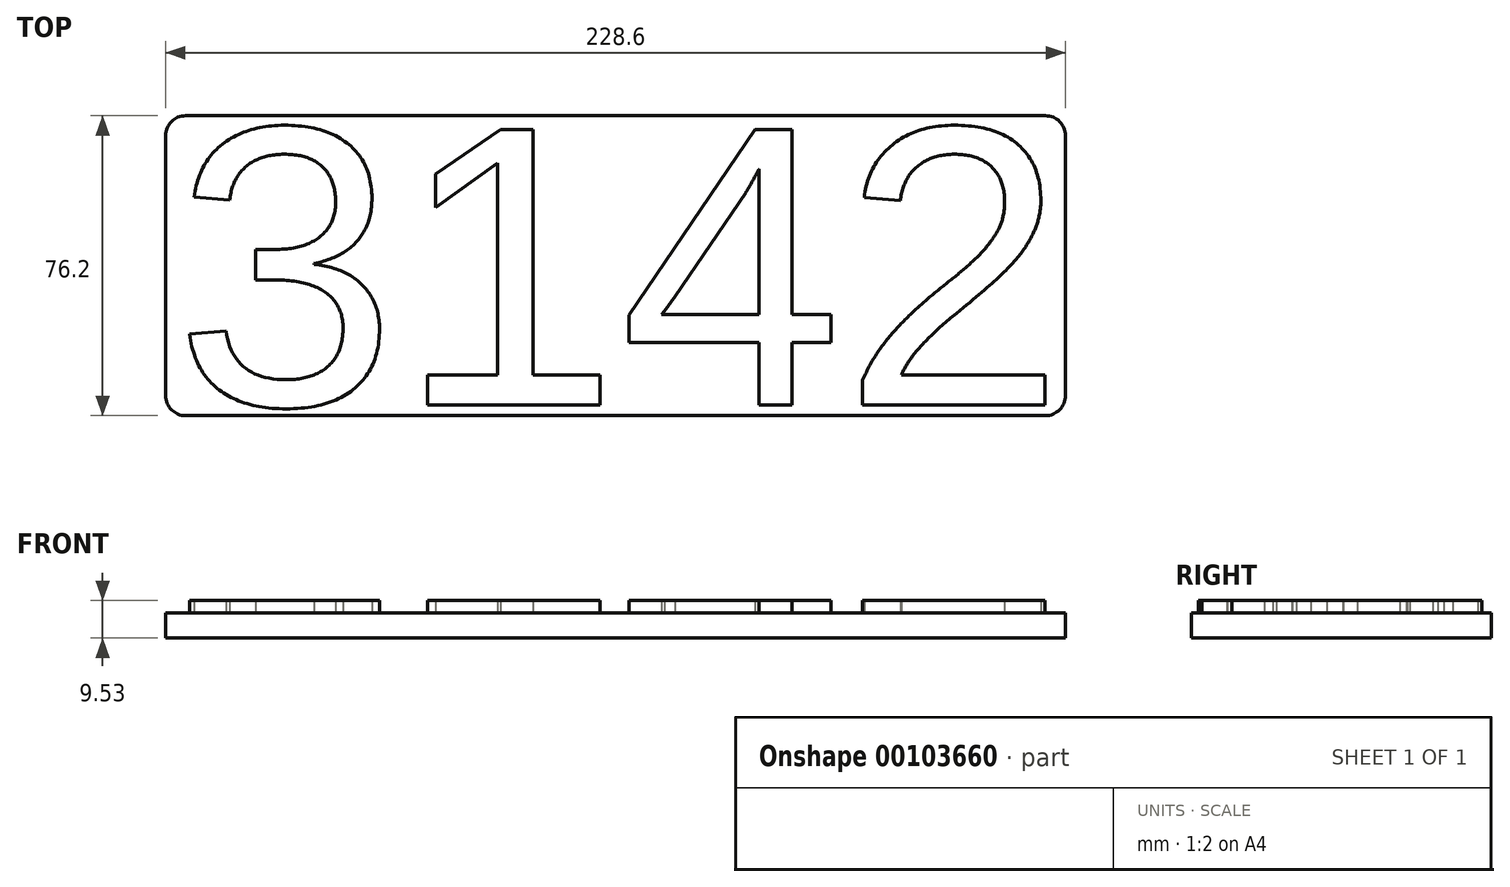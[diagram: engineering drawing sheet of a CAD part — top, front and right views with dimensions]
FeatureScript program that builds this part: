
annotation { "Feature Type Name" : "Feature", "Feature Type Description" : "" }
export const myFeature = defineFeature(function(context is Context, id is Id, definition is map)
    precondition{}
    {
        {
            var Q0;
            Q0=qCreatedBy(makeId("Top.planeOp"),FACE);
            var sketch = newSketch(context, id + "F0", { "sketchPlane" : qUnion([Q0])});
            skLineSegment(sketch, "E0.bottom", {"start": v(-101.24, 50.27) * mm, "end": v(127.36, 50.27) * mm});
            skLineSegment(sketch, "E0.top", {"start": v(-101.24, -25.93) * mm, "end": v(127.36, -25.93) * mm});
            skLineSegment(sketch, "E0.left", {"start": v(-101.24, 50.27) * mm, "end": v(-101.24, -25.93) * mm});
            skLineSegment(sketch, "E0.right", {"start": v(127.36, 50.27) * mm, "end": v(127.36, -25.93) * mm});
            skSolve(sketch);
        }
        {
            var Q0;
            Q0 = qSketchRegion(id + "F0", true);
            extrude(context, id + "F1", {"entities" : qUnion([Q0]), "depth" : 6.35 * mm});
        }
        {
            var Q0;
            Q0=makeQuery(id+"F1.opExtrude","CAP_FACE",FACE,{"disambiguationData":[OSD([sQuery(id+"F0.wireOp",EDGE,"E0.bottom"),sQuery(id+"F0.wireOp",EDGE,"E0.top"),sQuery(id+"F0.wireOp",EDGE,"E0.left"),sQuery(id+"F0.wireOp",EDGE,"E0.right")])],"isStart":false});
            var sketch = newSketch(context, id + "F2", { "sketchPlane" : qUnion([Q0])});
            skText(sketch, "E1", { "text": "3142", "fontName": "Arimo-Regular.ttf"});
            const initialGuessF2  = {"E1": [-0.09902, -0.0232, 1, 0, 0.07326]};
            skSetInitialGuess(sketch, initialGuessF2);
            skSolve(sketch);
        }
        {
            var Q0;
            Q0 = qSketchRegion(id + "F2", true);
            extrude(context, id + "F3", {"entities" : qUnion([Q0]), "operationType" : NewBodyOperationType.ADD, "depth" : 3.17 * mm});
        }
        {
            var Q0;
            Q0=makeQuery(id+"F1.opExtrude","SWEPT_EDGE",EDGE,{"disambiguationData":[OSD([sQuery(id+"F0.wireOp",EDGE,"E0.top"),sQuery(id+"F0.wireOp",EDGE,"E0.right")])]});
            var Q1;
            Q1=makeQuery(id+"F1.opExtrude","SWEPT_EDGE",EDGE,{"disambiguationData":[OSD([sQuery(id+"F0.wireOp",EDGE,"E0.bottom"),sQuery(id+"F0.wireOp",EDGE,"E0.right")])]});
            var Q2;
            Q2=makeQuery(id+"F1.opExtrude","SWEPT_EDGE",EDGE,{"disambiguationData":[OSD([sQuery(id+"F0.wireOp",EDGE,"E0.bottom"),sQuery(id+"F0.wireOp",EDGE,"E0.left")])]});
            var Q3;
            Q3=makeQuery(id+"F1.opExtrude","SWEPT_EDGE",EDGE,{"disambiguationData":[OSD([sQuery(id+"F0.wireOp",EDGE,"E0.top"),sQuery(id+"F0.wireOp",EDGE,"E0.left")])]});
            fillet(context, id + "F4", {"entities" : qUnion([Q0, Q1, Q2, Q3]), "radius" : 5.08 * mm, "tangentPropagation" : true, "allowEdgeOverflow" : false});
        }
    });
